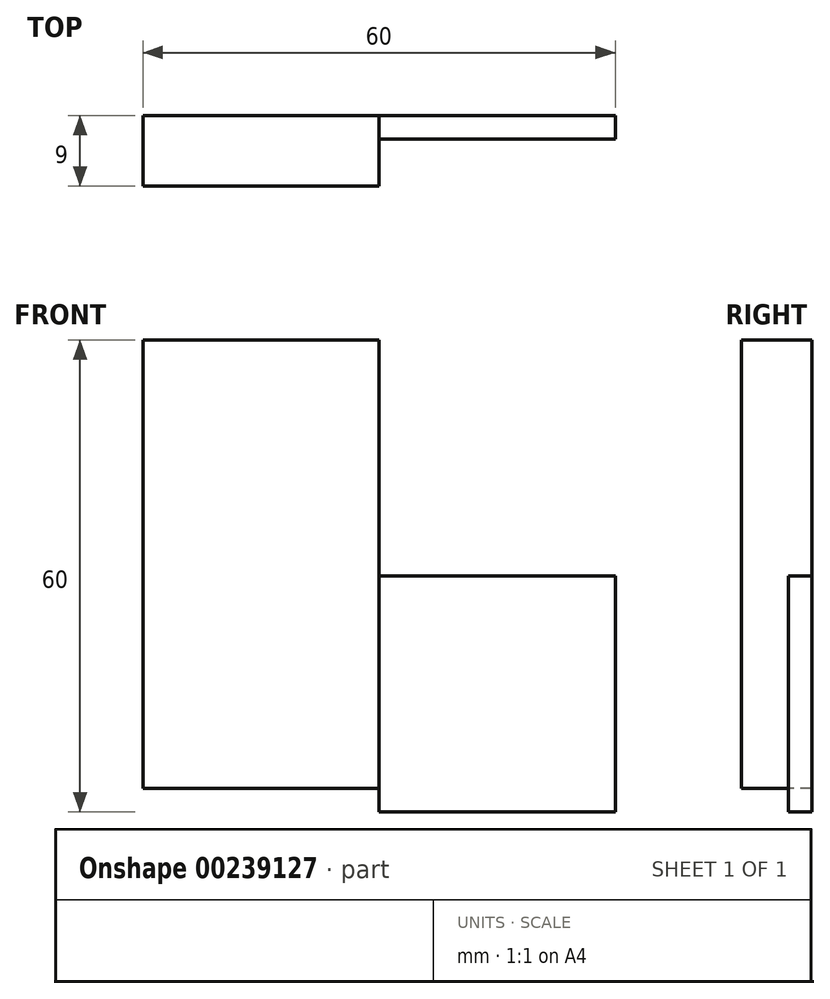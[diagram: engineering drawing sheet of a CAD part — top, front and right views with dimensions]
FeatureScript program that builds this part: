
annotation { "Feature Type Name" : "Feature", "Feature Type Description" : "" }
export const myFeature = defineFeature(function(context is Context, id is Id, definition is map)
    precondition{}
    {
        {
            assignVariable(context, id + "F0", {"name" : "e", "anyValue" : 3});
        }
        {
            var Q0;
            Q0=qCreatedBy(makeId("Front.planeOp"),FACE);
            var sketch = newSketch(context, id + "F1", { "sketchPlane" : qUnion([Q0])});
            skLineSegment(sketch, "E0.bottom", {"start": v(30, 30) * mm, "end": v(-30, 30) * mm});
            skLineSegment(sketch, "E0.top", {"start": v(30, -30) * mm, "end": v(-30, -30) * mm});
            skLineSegment(sketch, "E0.left", {"start": v(30, 30) * mm, "end": v(30, -30) * mm});
            skLineSegment(sketch, "E0.right", {"start": v(-30, 30) * mm, "end": v(-30, -30) * mm});
            skPoint(sketch, "E0.middle", {"position": v(0, 0) * mm});
            skSolve(sketch);
        }
        {
            var Q0;
            Q0 = qSketchRegion(id + "F1", true);
            extrude(context, id + "F2", {"entities" : qUnion([Q0]), "endBound" : BoundingType.SYMMETRIC, "depth" : (3 * getVariable(context, 'e')) * mm});
        }
        {
            var Q0;
            Q0=makeQuery(id+"F2.opExtrude","CAP_FACE",FACE,{"disambiguationData":[OSD([sQuery(id+"F1.wireOp",EDGE,"E0.bottom"),sQuery(id+"F1.wireOp",EDGE,"E0.top"),sQuery(id+"F1.wireOp",EDGE,"E0.left"),sQuery(id+"F1.wireOp",EDGE,"E0.right")])],"isStart":false});
            var sketch = newSketch(context, id + "F3", { "sketchPlane" : qUnion([Q0])});
            skLineSegment(sketch, "E1.bottom", {"start": v(30, 30) * mm, "end": v(0, 30) * mm});
            skLineSegment(sketch, "E1.top", {"start": v(30, 0) * mm, "end": v(0, 0) * mm});
            skLineSegment(sketch, "E1.left", {"start": v(30, 30) * mm, "end": v(30, 0) * mm});
            skLineSegment(sketch, "E1.right", {"start": v(0, 30) * mm, "end": v(0, 0) * mm});
            skSolve(sketch);
        }
        {
            var Q0;
            Q0 = qSketchRegion(id + "F3", true);
            extrude(context, id + "F4", {"entities" : qUnion([Q0]), "operationType" : NewBodyOperationType.REMOVE, "endBound" : BoundingType.THROUGH_ALL, "oppositeDirection" : true, "depth" : 25 * mm});
        }
        {
            var Q0;
            Q0=makeQuery(id+"F2.opExtrude","CAP_FACE",FACE,{"disambiguationData":[OSD([sQuery(id+"F1.wireOp",EDGE,"E0.bottom"),sQuery(id+"F1.wireOp",EDGE,"E0.top"),sQuery(id+"F1.wireOp",EDGE,"E0.left"),sQuery(id+"F1.wireOp",EDGE,"E0.right")])],"isStart":false});
            var sketch = newSketch(context, id + "F5", { "sketchPlane" : qUnion([Q0])});
            skLineSegment(sketch, "E2.bottom", {"start": v(0, 0) * mm, "end": v(30, 0) * mm});
            skLineSegment(sketch, "E2.top", {"start": v(0, -30) * mm, "end": v(30, -30) * mm});
            skLineSegment(sketch, "E2.left", {"start": v(0, 0) * mm, "end": v(0, -30) * mm});
            skLineSegment(sketch, "E2.right", {"start": v(30, 0) * mm, "end": v(30, -30) * mm});
            skSolve(sketch);
        }
        {
            var Q0;
            Q0 = qSketchRegion(id + "F5", true);
            extrude(context, id + "F6", {"entities" : qUnion([Q0]), "operationType" : NewBodyOperationType.REMOVE, "oppositeDirection" : true, "depth" : (2 * getVariable(context, 'e')) * mm});
        }
        {
            var Q0;
            Q0=makeQuery(id+"F2.opExtrude","SWEPT_FACE",FACE,{"disambiguationData":[OSD([sQuery(id+"F1.wireOp",EDGE,"E0.top")])]});
            var sketch = newSketch(context, id + "F7", { "sketchPlane" : qUnion([Q0])});
            skLineSegment(sketch, "E3.bottom", {"start": v(0, -15) * mm, "end": v(-30, -15) * mm, "construction": true});
            skLineSegment(sketch, "E3.top", {"start": v(0, -45) * mm, "end": v(-30, -45) * mm, "construction": true});
            skLineSegment(sketch, "E3.left", {"start": v(0, -15) * mm, "end": v(0, -45) * mm, "construction": true});
            skLineSegment(sketch, "E3.right", {"start": v(-30, -15) * mm, "end": v(-30, -45) * mm, "construction": true});
            skPoint(sketch, "E4.oppositeSnap0", {"position": v(0, 15) * mm});
            skLineSegment(sketch, "E4.bottom", {"start": v(0, -15) * mm, "end": v(-30, -15) * mm});
            skLineSegment(sketch, "E4.top", {"start": v(0, 15) * mm, "end": v(-30, 15) * mm});
            skLineSegment(sketch, "E4.left", {"start": v(0, -15) * mm, "end": v(0, 15) * mm});
            skLineSegment(sketch, "E4.right", {"start": v(-30, -15) * mm, "end": v(-30, 15) * mm});
            skSolve(sketch);
        }
        {
            var Q0;
            Q0 = qSketchRegion(id + "F7", true);
            extrude(context, id + "F8", {"entities" : qUnion([Q0]), "operationType" : NewBodyOperationType.REMOVE, "oppositeDirection" : true, "depth" : (getVariable(context, 'e')) * mm});
        }
    });
